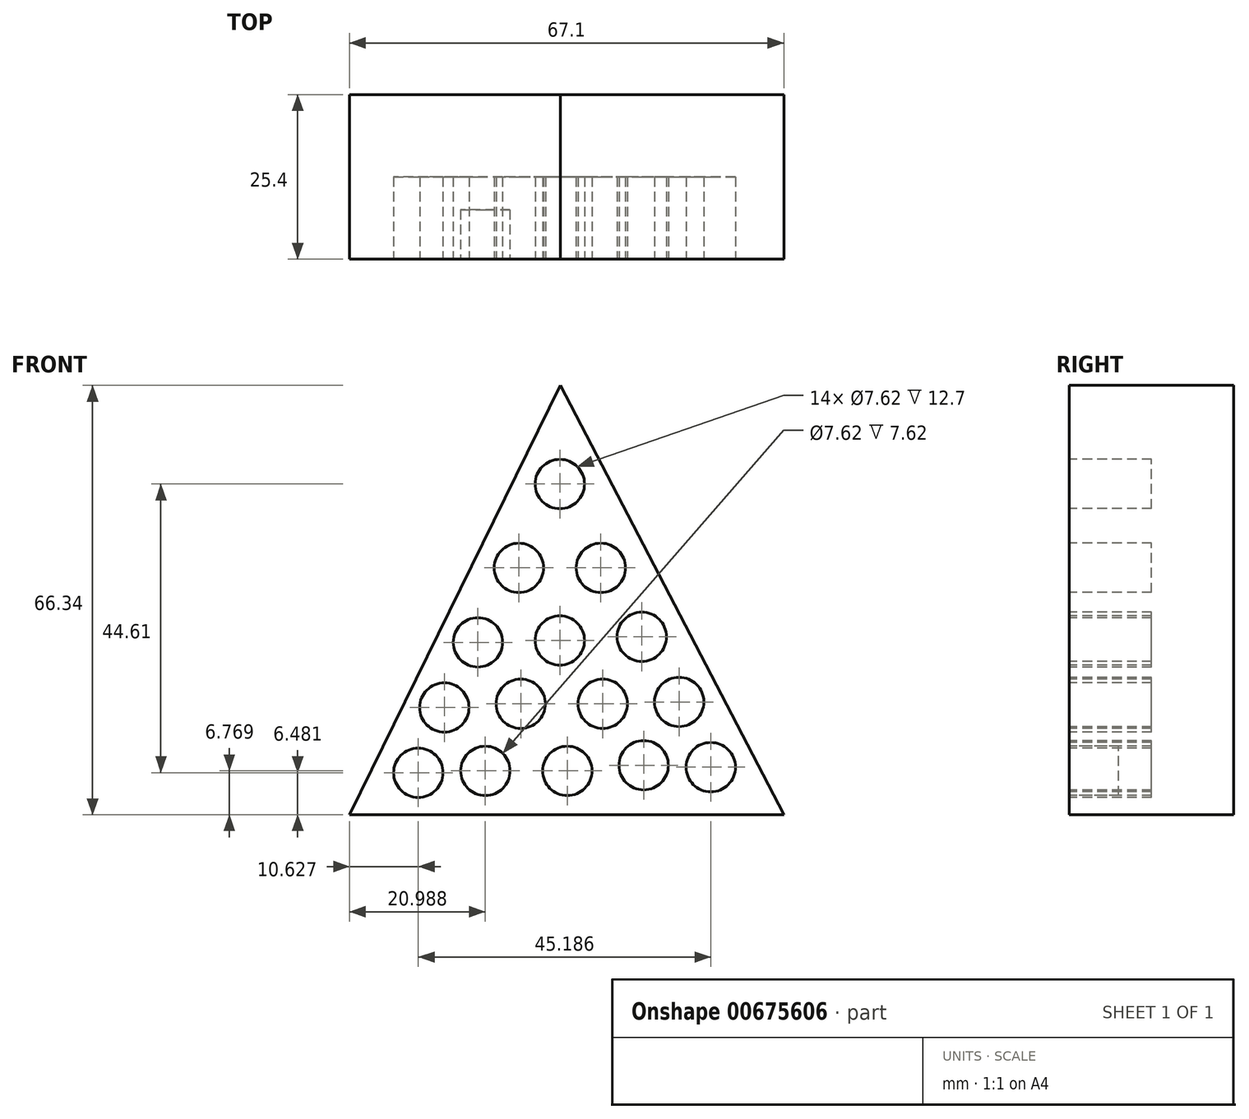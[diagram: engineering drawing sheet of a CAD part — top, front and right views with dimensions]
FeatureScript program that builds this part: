
annotation { "Feature Type Name" : "Feature", "Feature Type Description" : "" }
export const myFeature = defineFeature(function(context is Context, id is Id, definition is map)
    precondition{}
    {
        {
            var Q0;
            Q0=qCreatedBy(makeId("Front.planeOp"),FACE);
            var sketch = newSketch(context, id + "F0", { "sketchPlane" : qUnion([Q0])});
            skLineSegment(sketch, "E0", {"start": v(0, 0) * mm, "end": v(-39.57, 76.12) * mm});
            skLineSegment(sketch, "E1", {"start": v(-39.57, 76.12) * mm, "end": v(-76.99, 0) * mm});
            skLineSegment(sketch, "E2", {"start": v(-76.99, 0) * mm, "end": v(0, 0) * mm});
            skSolve(sketch);
        }
        {
            var Q0;
            Q0 = qSketchRegion(id + "F0", true);
            extrude(context, id + "F1", {"entities" : qUnion([Q0]), "depth" : 25.4 * mm, "offsetDistance" : 25.4 * mm});
        }
        {
            var Q0;
            Q0=makeQuery(id+"F1.opExtrude","CAP_FACE",FACE,{"disambiguationData":[OSD([sQuery(id+"F0.wireOp",EDGE,"E0"),sQuery(id+"F0.wireOp",EDGE,"E1"),sQuery(id+"F0.wireOp",EDGE,"E2")])],"isStart":false});
            var sketch = newSketch(context, id + "F2", { "sketchPlane" : qUnion([Q0])});
            skCircle(sketch, "E3", {"center": v(-39.68, 60.87) * mm, "radius": 3.81 * mm});
            skSolve(sketch);
        }
        {
            var Q0;
            Q0 = qSketchRegion(id + "F2", true);
            extrude(context, id + "F3", {"entities" : qUnion([Q0]), "operationType" : NewBodyOperationType.REMOVE, "oppositeDirection" : true, "depth" : 12.7 * mm, "offsetDistance" : 25.4 * mm});
        }
        {
            var Q0;
            Q0=makeQuery(id+"F1.opExtrude","CAP_FACE",FACE,{"disambiguationData":[OSD([sQuery(id+"F0.wireOp",EDGE,"E0"),sQuery(id+"F0.wireOp",EDGE,"E1"),sQuery(id+"F0.wireOp",EDGE,"E2")])],"isStart":false});
            var sketch = newSketch(context, id + "F4", { "sketchPlane" : qUnion([Q0])});
            skCircle(sketch, "E4", {"center": v(-46.01, 47.92) * mm, "radius": 3.81 * mm});
            skSolve(sketch);
        }
        {
            var Q0;
            Q0 = qSketchRegion(id + "F4", true);
            extrude(context, id + "F5", {"entities" : qUnion([Q0]), "operationType" : NewBodyOperationType.REMOVE, "oppositeDirection" : true, "depth" : 12.7 * mm, "offsetDistance" : 25.4 * mm});
        }
        {
            var Q0;
            Q0=makeQuery(id+"F1.opExtrude","CAP_FACE",FACE,{"disambiguationData":[OSD([sQuery(id+"F0.wireOp",EDGE,"E0"),sQuery(id+"F0.wireOp",EDGE,"E1"),sQuery(id+"F0.wireOp",EDGE,"E2")])],"isStart":false});
            var sketch = newSketch(context, id + "F6", { "sketchPlane" : qUnion([Q0])});
            skCircle(sketch, "E5", {"center": v(-33.35, 47.92) * mm, "radius": 3.81 * mm});
            skSolve(sketch);
        }
        {
            var Q0;
            Q0 = qSketchRegion(id + "F6", true);
            extrude(context, id + "F7", {"entities" : qUnion([Q0]), "operationType" : NewBodyOperationType.REMOVE, "oppositeDirection" : true, "depth" : 12.7 * mm, "offsetDistance" : 25.4 * mm});
        }
        {
            var Q0;
            Q0=makeQuery(id+"F1.opExtrude","CAP_FACE",FACE,{"disambiguationData":[OSD([sQuery(id+"F0.wireOp",EDGE,"E0"),sQuery(id+"F0.wireOp",EDGE,"E1"),sQuery(id+"F0.wireOp",EDGE,"E2")])],"isStart":false});
            var sketch = newSketch(context, id + "F8", { "sketchPlane" : qUnion([Q0])});
            skCircle(sketch, "E6", {"center": v(-52.34, 36.4) * mm, "radius": 3.81 * mm});
            skSolve(sketch);
        }
        {
            var Q0;
            Q0 = qSketchRegion(id + "F8", true);
            extrude(context, id + "F9", {"entities" : qUnion([Q0]), "operationType" : NewBodyOperationType.REMOVE, "oppositeDirection" : true, "depth" : 12.7 * mm, "offsetDistance" : 25.4 * mm});
        }
        {
            var Q0;
            Q0=makeQuery(id+"F1.opExtrude","CAP_FACE",FACE,{"disambiguationData":[OSD([sQuery(id+"F0.wireOp",EDGE,"E0"),sQuery(id+"F0.wireOp",EDGE,"E1"),sQuery(id+"F0.wireOp",EDGE,"E2")])],"isStart":false});
            var sketch = newSketch(context, id + "F10", { "sketchPlane" : qUnion([Q0])});
            skCircle(sketch, "E7", {"center": v(-39.68, 36.7) * mm, "radius": 3.81 * mm});
            skSolve(sketch);
        }
        {
            var Q0;
            Q0 = qSketchRegion(id + "F10", true);
            extrude(context, id + "F11", {"entities" : qUnion([Q0]), "operationType" : NewBodyOperationType.REMOVE, "oppositeDirection" : true, "depth" : 12.7 * mm, "offsetDistance" : 25.4 * mm});
        }
        {
            var Q0;
            Q0=makeQuery(id+"F1.opExtrude","CAP_FACE",FACE,{"disambiguationData":[OSD([sQuery(id+"F0.wireOp",EDGE,"E0"),sQuery(id+"F0.wireOp",EDGE,"E1"),sQuery(id+"F0.wireOp",EDGE,"E2")])],"isStart":false});
            var sketch = newSketch(context, id + "F12", { "sketchPlane" : qUnion([Q0])});
            skCircle(sketch, "E8", {"center": v(-27.02, 37.27) * mm, "radius": 3.81 * mm});
            skSolve(sketch);
        }
        {
            var Q0;
            Q0 = qSketchRegion(id + "F12", true);
            extrude(context, id + "F13", {"entities" : qUnion([Q0]), "operationType" : NewBodyOperationType.REMOVE, "oppositeDirection" : true, "depth" : 12.7 * mm, "offsetDistance" : 25.4 * mm});
        }
        {
            var Q0;
            Q0=makeQuery(id+"F1.opExtrude","CAP_FACE",FACE,{"disambiguationData":[OSD([sQuery(id+"F0.wireOp",EDGE,"E0"),sQuery(id+"F0.wireOp",EDGE,"E1"),sQuery(id+"F0.wireOp",EDGE,"E2")])],"isStart":false});
            var sketch = newSketch(context, id + "F14", { "sketchPlane" : qUnion([Q0])});
            skCircle(sketch, "E9", {"center": v(-57.52, 26.33) * mm, "radius": 3.81 * mm});
            skSolve(sketch);
        }
        {
            var Q0;
            Q0 = qSketchRegion(id + "F14", true);
            extrude(context, id + "F15", {"entities" : qUnion([Q0]), "operationType" : NewBodyOperationType.REMOVE, "oppositeDirection" : true, "depth" : 12.7 * mm, "offsetDistance" : 25.4 * mm});
        }
        {
            var Q0;
            Q0=makeQuery(id+"F1.opExtrude","CAP_FACE",FACE,{"disambiguationData":[OSD([sQuery(id+"F0.wireOp",EDGE,"E0"),sQuery(id+"F0.wireOp",EDGE,"E1"),sQuery(id+"F0.wireOp",EDGE,"E2")])],"isStart":false});
            var sketch = newSketch(context, id + "F16", { "sketchPlane" : qUnion([Q0])});
            skCircle(sketch, "E10", {"center": v(-45.72, 26.9) * mm, "radius": 3.81 * mm});
            skSolve(sketch);
        }
        {
            var Q0;
            Q0 = qSketchRegion(id + "F16", true);
            extrude(context, id + "F17", {"entities" : qUnion([Q0]), "operationType" : NewBodyOperationType.REMOVE, "oppositeDirection" : true, "depth" : 12.7 * mm, "offsetDistance" : 25.4 * mm});
        }
        {
            var Q0;
            Q0=makeQuery(id+"F1.opExtrude","CAP_FACE",FACE,{"disambiguationData":[OSD([sQuery(id+"F0.wireOp",EDGE,"E0"),sQuery(id+"F0.wireOp",EDGE,"E1"),sQuery(id+"F0.wireOp",EDGE,"E2")])],"isStart":false});
            var sketch = newSketch(context, id + "F18", { "sketchPlane" : qUnion([Q0])});
            skCircle(sketch, "E11", {"center": v(-33.06, 26.9) * mm, "radius": 3.81 * mm});
            skSolve(sketch);
        }
        {
            var Q0;
            Q0 = qSketchRegion(id + "F18", true);
            extrude(context, id + "F19", {"entities" : qUnion([Q0]), "operationType" : NewBodyOperationType.REMOVE, "oppositeDirection" : true, "depth" : 12.7 * mm, "offsetDistance" : 25.4 * mm});
        }
        {
            var Q0;
            Q0=makeQuery(id+"F1.opExtrude","CAP_FACE",FACE,{"disambiguationData":[OSD([sQuery(id+"F0.wireOp",EDGE,"E0"),sQuery(id+"F0.wireOp",EDGE,"E1"),sQuery(id+"F0.wireOp",EDGE,"E2")])],"isStart":false});
            var sketch = newSketch(context, id + "F20", { "sketchPlane" : qUnion([Q0])});
            skCircle(sketch, "E12", {"center": v(-21.26, 27.2) * mm, "radius": 3.81 * mm});
            skSolve(sketch);
        }
        {
            var Q0;
            Q0 = qSketchRegion(id + "F20", true);
            extrude(context, id + "F21", {"entities" : qUnion([Q0]), "operationType" : NewBodyOperationType.REMOVE, "oppositeDirection" : true, "depth" : 12.7 * mm, "offsetDistance" : 25.4 * mm});
        }
        {
            var Q0;
            Q0=makeQuery(id+"F1.opExtrude","CAP_FACE",FACE,{"disambiguationData":[OSD([sQuery(id+"F0.wireOp",EDGE,"E0"),sQuery(id+"F0.wireOp",EDGE,"E1"),sQuery(id+"F0.wireOp",EDGE,"E2")])],"isStart":false});
            var sketch = newSketch(context, id + "F22", { "sketchPlane" : qUnion([Q0])});
            skCircle(sketch, "E13", {"center": v(-61.55, 16.26) * mm, "radius": 3.81 * mm});
            skSolve(sketch);
        }
        {
            var Q0;
            Q0 = qSketchRegion(id + "F22", true);
            extrude(context, id + "F23", {"entities" : qUnion([Q0]), "operationType" : NewBodyOperationType.REMOVE, "oppositeDirection" : true, "depth" : 12.7 * mm, "offsetDistance" : 25.4 * mm});
        }
        {
            var Q0;
            Q0=makeQuery(id+"F1.opExtrude","CAP_FACE",FACE,{"disambiguationData":[OSD([sQuery(id+"F0.wireOp",EDGE,"E0"),sQuery(id+"F0.wireOp",EDGE,"E1"),sQuery(id+"F0.wireOp",EDGE,"E2")])],"isStart":false});
            var sketch = newSketch(context, id + "F24", { "sketchPlane" : qUnion([Q0])});
            skCircle(sketch, "E14", {"center": v(-51.2, 16.55) * mm, "radius": 3.81 * mm});
            skSolve(sketch);
        }
        {
            var Q0;
            Q0 = qSketchRegion(id + "F24", true);
            extrude(context, id + "F25", {"entities" : qUnion([Q0]), "operationType" : NewBodyOperationType.REMOVE, "oppositeDirection" : true, "depth" : 7.62 * mm, "offsetDistance" : 25.4 * mm});
        }
        {
            var Q0;
            Q0=makeQuery(id+"F1.opExtrude","CAP_FACE",FACE,{"disambiguationData":[OSD([sQuery(id+"F0.wireOp",EDGE,"E0"),sQuery(id+"F0.wireOp",EDGE,"E1"),sQuery(id+"F0.wireOp",EDGE,"E2")])],"isStart":false});
            var sketch = newSketch(context, id + "F26", { "sketchPlane" : qUnion([Q0])});
            skCircle(sketch, "E15", {"center": v(-38.53, 16.55) * mm, "radius": 3.81 * mm});
            skSolve(sketch);
        }
        {
            var Q0;
            Q0 = qSketchRegion(id + "F26", true);
            extrude(context, id + "F27", {"entities" : qUnion([Q0]), "operationType" : NewBodyOperationType.REMOVE, "oppositeDirection" : true, "depth" : 12.7 * mm, "offsetDistance" : 25.4 * mm});
        }
        {
            var Q0;
            Q0=makeQuery(id+"F1.opExtrude","CAP_FACE",FACE,{"disambiguationData":[OSD([sQuery(id+"F0.wireOp",EDGE,"E0"),sQuery(id+"F0.wireOp",EDGE,"E1"),sQuery(id+"F0.wireOp",EDGE,"E2")])],"isStart":false});
            var sketch = newSketch(context, id + "F28", { "sketchPlane" : qUnion([Q0])});
            skCircle(sketch, "E16", {"center": v(-26.73, 17.41) * mm, "radius": 3.81 * mm});
            skSolve(sketch);
        }
        {
            var Q0;
            Q0 = qSketchRegion(id + "F28", true);
            extrude(context, id + "F29", {"entities" : qUnion([Q0]), "operationType" : NewBodyOperationType.REMOVE, "oppositeDirection" : true, "depth" : 12.7 * mm, "offsetDistance" : 25.4 * mm});
        }
        {
            var Q0;
            Q0=makeQuery(id+"F1.opExtrude","CAP_FACE",FACE,{"disambiguationData":[OSD([sQuery(id+"F0.wireOp",EDGE,"E0"),sQuery(id+"F0.wireOp",EDGE,"E1"),sQuery(id+"F0.wireOp",EDGE,"E2")])],"isStart":false});
            var sketch = newSketch(context, id + "F30", { "sketchPlane" : qUnion([Q0])});
            skCircle(sketch, "E17", {"center": v(-16.37, 17.12) * mm, "radius": 3.81 * mm});
            skSolve(sketch);
        }
        {
            var Q0;
            Q0 = qSketchRegion(id + "F30", true);
            extrude(context, id + "F31", {"entities" : qUnion([Q0]), "operationType" : NewBodyOperationType.REMOVE, "oppositeDirection" : true, "depth" : 12.7 * mm, "offsetDistance" : 25.4 * mm});
        }
        {
            var Q0;
            Q0=makeQuery(id+"F1.opExtrude","CAP_FACE",FACE,{"disambiguationData":[OSD([sQuery(id+"F0.wireOp",EDGE,"E0"),sQuery(id+"F0.wireOp",EDGE,"E1"),sQuery(id+"F0.wireOp",EDGE,"E2")])],"isStart":false});
            var sketch = newSketch(context, id + "F32", { "sketchPlane" : qUnion([Q0])});
            skLineSegment(sketch, "E18", {"start": v(-72.18, 9.78) * mm, "end": v(-5.08, 9.78) * mm});
            skLineSegment(sketch, "E19", {"start": v(-5.08, 9.78) * mm, "end": v(0, 0) * mm});
            skLineSegment(sketch, "E20", {"start": v(0, 0) * mm, "end": v(-76.99, 0) * mm});
            skLineSegment(sketch, "E21", {"start": v(-76.99, 0) * mm, "end": v(-72.18, 9.78) * mm});
            skSolve(sketch);
        }
        {
            var Q0;
            Q0 = qSketchRegion(id + "F32", true);
            extrude(context, id + "F33", {"entities" : qUnion([Q0]), "operationType" : NewBodyOperationType.REMOVE, "oppositeDirection" : true, "depth" : 127 * mm, "offsetDistance" : 25.4 * mm});
        }
    });
